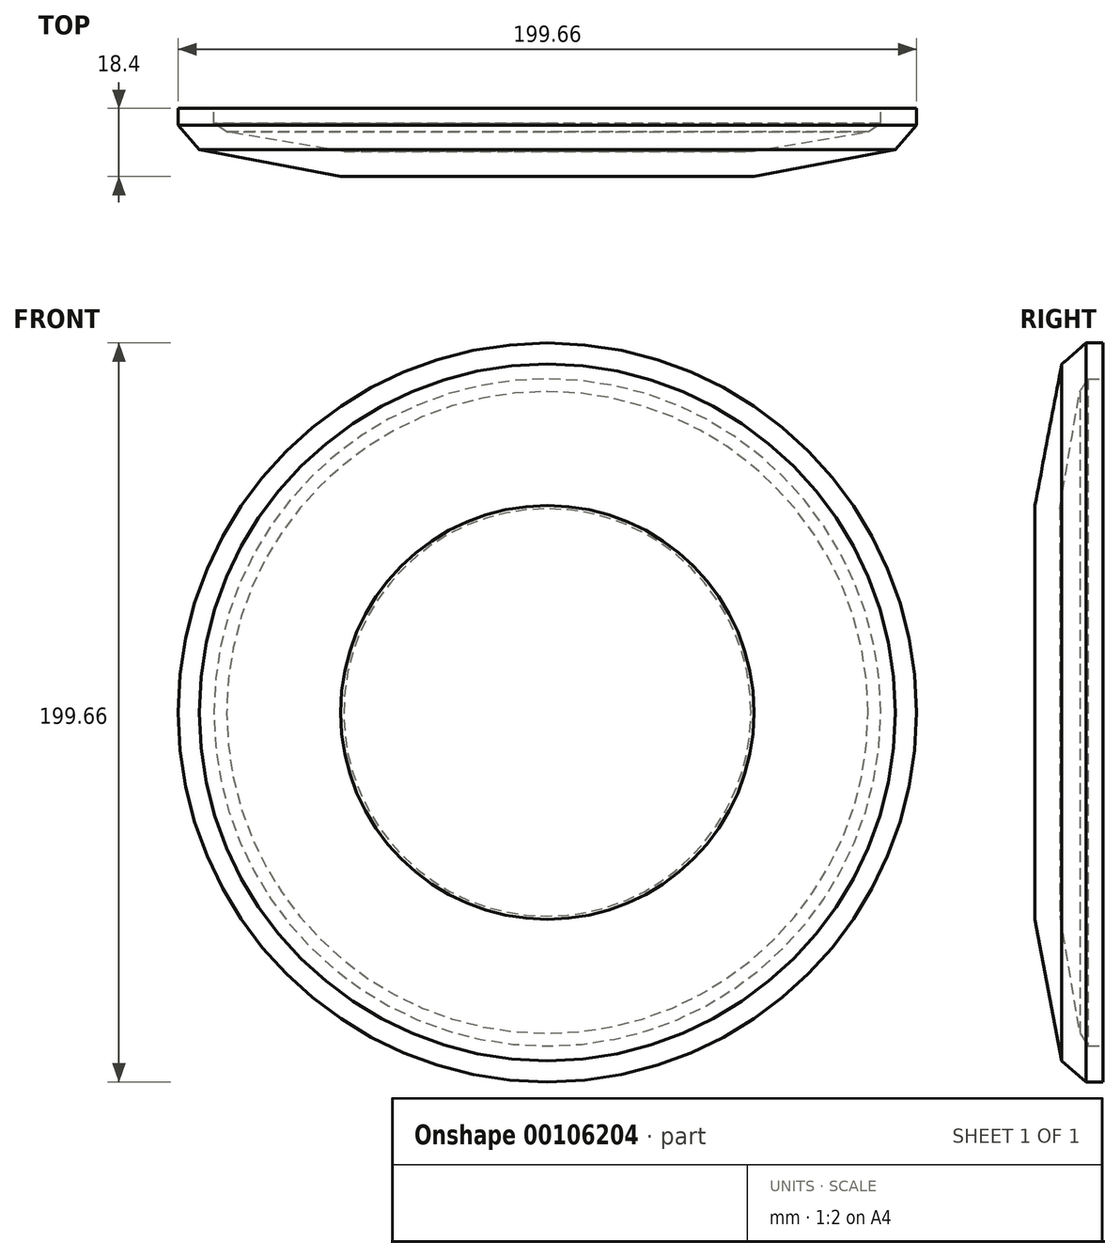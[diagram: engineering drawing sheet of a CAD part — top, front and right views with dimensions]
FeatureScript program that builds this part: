
annotation { "Feature Type Name" : "Feature", "Feature Type Description" : "" }
export const myFeature = defineFeature(function(context is Context, id is Id, definition is map)
    precondition{}
    {
        {
            var Q0;
            Q0=qCreatedBy(makeId("Top.planeOp"),FACE);
            var sketch = newSketch(context, id + "F0", { "sketchPlane" : qUnion([Q0])});
            skLineSegment(sketch, "E0", {"start": v(0, 0) * mm, "end": v(-55.9, 0) * mm});
            skLineSegment(sketch, "E1", {"start": v(-55.9, 0) * mm, "end": v(-94.13, 7.27) * mm});
            skLineSegment(sketch, "E2", {"start": v(-94.13, 7.27) * mm, "end": v(-99.83, 13.83) * mm});
            skLineSegment(sketch, "E3", {"start": v(-99.83, 13.83) * mm, "end": v(-99.83, 18.4) * mm});
            skLineSegment(sketch, "E4", {"start": v(-99.83, 18.4) * mm, "end": v(-90.14, 18.4) * mm});
            skLineSegment(sketch, "E5", {"start": v(-90.14, 18.4) * mm, "end": v(-90.14, 14.4) * mm});
            skLineSegment(sketch, "E6", {"start": v(-90.14, 14.4) * mm, "end": v(-86.71, 12.12) * mm});
            skLineSegment(sketch, "E7", {"start": v(-86.71, 12.12) * mm, "end": v(-55.05, 6.7) * mm});
            skLineSegment(sketch, "E8", {"start": v(-55.05, 6.7) * mm, "end": v(0, 6.7) * mm});
            skLineSegment(sketch, "E9", {"start": v(0, 6.7) * mm, "end": v(0, 0) * mm});
            skSolve(sketch);
        }
        {
            var Q0;
            Q0=makeQuery(id+"F0.imprint","IMPRINT",FACE,{"disambiguationData":[TD([[makeQuery(id+"F0.imprint","IMPRINT",EDGE,{"derivedFrom":sQuery(id+"F0.wireOp",EDGE,"E0")}),-1.0]])]});
            var Q1;
            Q1=sQuery(id+"F0.wireOp",EDGE,"E9");
            revolve(context, id + "F1", {"entities" : qUnion([Q0]), "axis" : qUnion([Q1]), "revolveType" : RevolveType.FULL});
        }
    });
